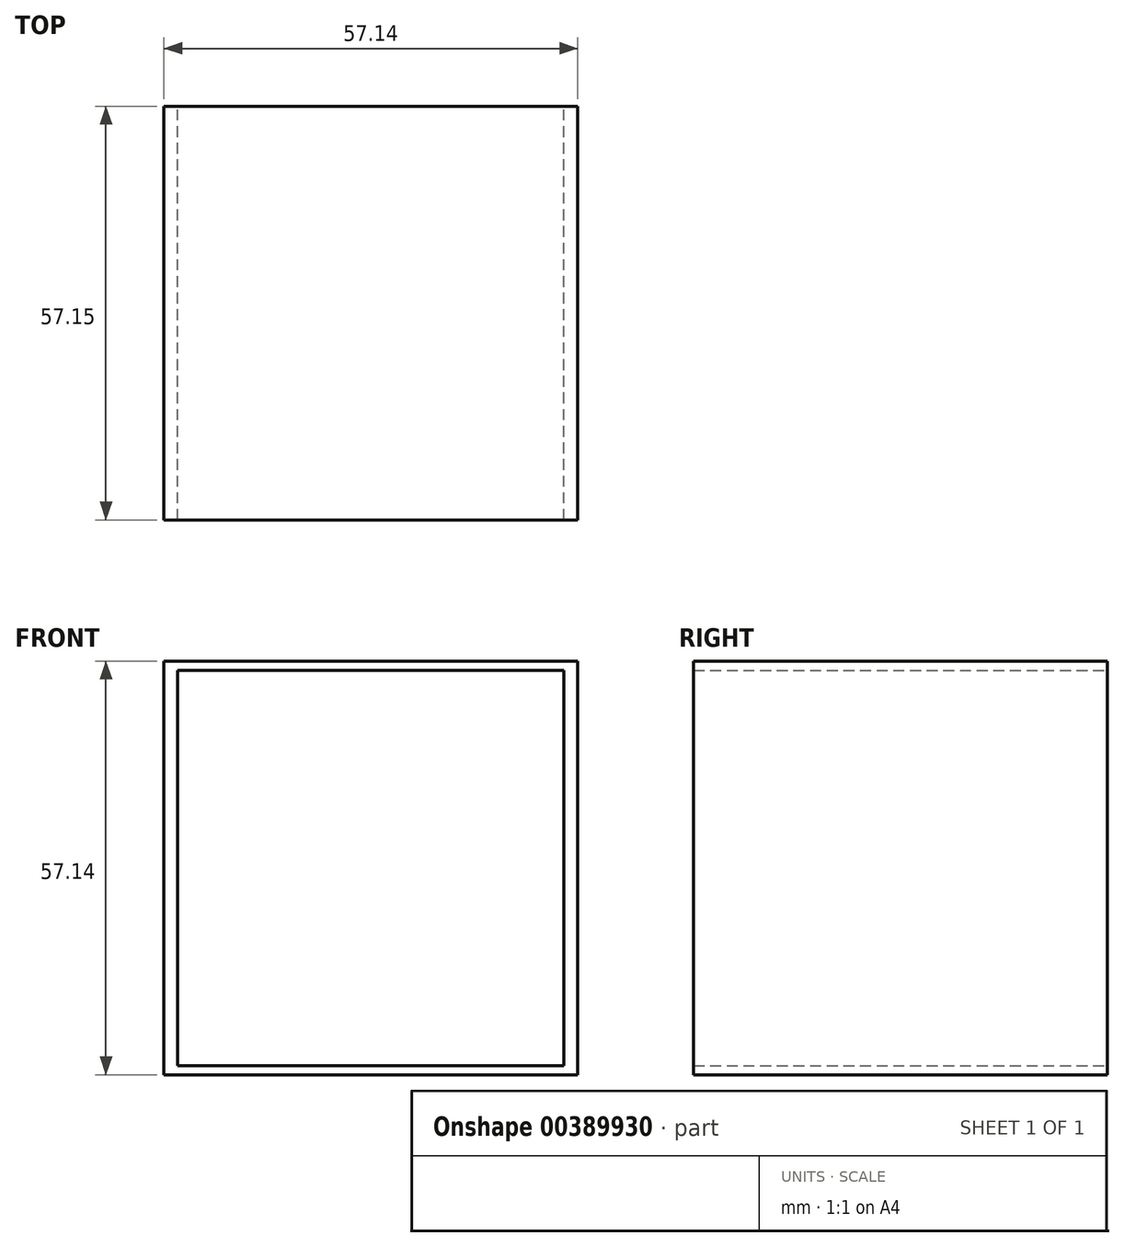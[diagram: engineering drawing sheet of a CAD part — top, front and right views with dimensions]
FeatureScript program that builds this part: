
annotation { "Feature Type Name" : "Feature", "Feature Type Description" : "" }
export const myFeature = defineFeature(function(context is Context, id is Id, definition is map)
    precondition{}
    {
        {
            var Q0;
            Q0=qCreatedBy(makeId("Front.planeOp"),FACE);
            var sketch = newSketch(context, id + "F0", { "sketchPlane" : qUnion([Q0])});
            skLineSegment(sketch, "E0.bottom", {"start": v(26.67, -27.3) * mm, "end": v(-26.67, -27.3) * mm});
            skLineSegment(sketch, "E0.top", {"start": v(26.67, 27.3) * mm, "end": v(-26.67, 27.3) * mm});
            skLineSegment(sketch, "E0.left", {"start": v(26.67, -27.3) * mm, "end": v(26.67, 27.3) * mm});
            skLineSegment(sketch, "E0.right", {"start": v(-26.67, -27.3) * mm, "end": v(-26.67, 27.3) * mm});
            skPoint(sketch, "E0.middle", {"position": v(0, 0) * mm});
            skLineSegment(sketch, "E1.bottom", {"start": v(28.57, -28.57) * mm, "end": v(-28.58, -28.58) * mm});
            skLineSegment(sketch, "E1.top", {"start": v(28.58, 28.58) * mm, "end": v(-28.58, 28.57) * mm});
            skLineSegment(sketch, "E1.left", {"start": v(28.57, -28.57) * mm, "end": v(28.58, 28.58) * mm});
            skLineSegment(sketch, "E1.right", {"start": v(-28.58, -28.58) * mm, "end": v(-28.58, 28.57) * mm});
            skSolve(sketch);
        }
        {
            var Q0;
            Q0=makeQuery(id+"F0.imprint","IMPRINT",FACE,{"disambiguationData":[TD([[makeQuery(id+"F0.imprint","IMPRINT",EDGE,{"derivedFrom":sQuery(id+"F0.wireOp",EDGE,"E0.bottom")}),1.0]])]});
            extrude(context, id + "F1", {"entities" : qUnion([Q0]), "depth" : 57.15 * mm});
        }
    });
